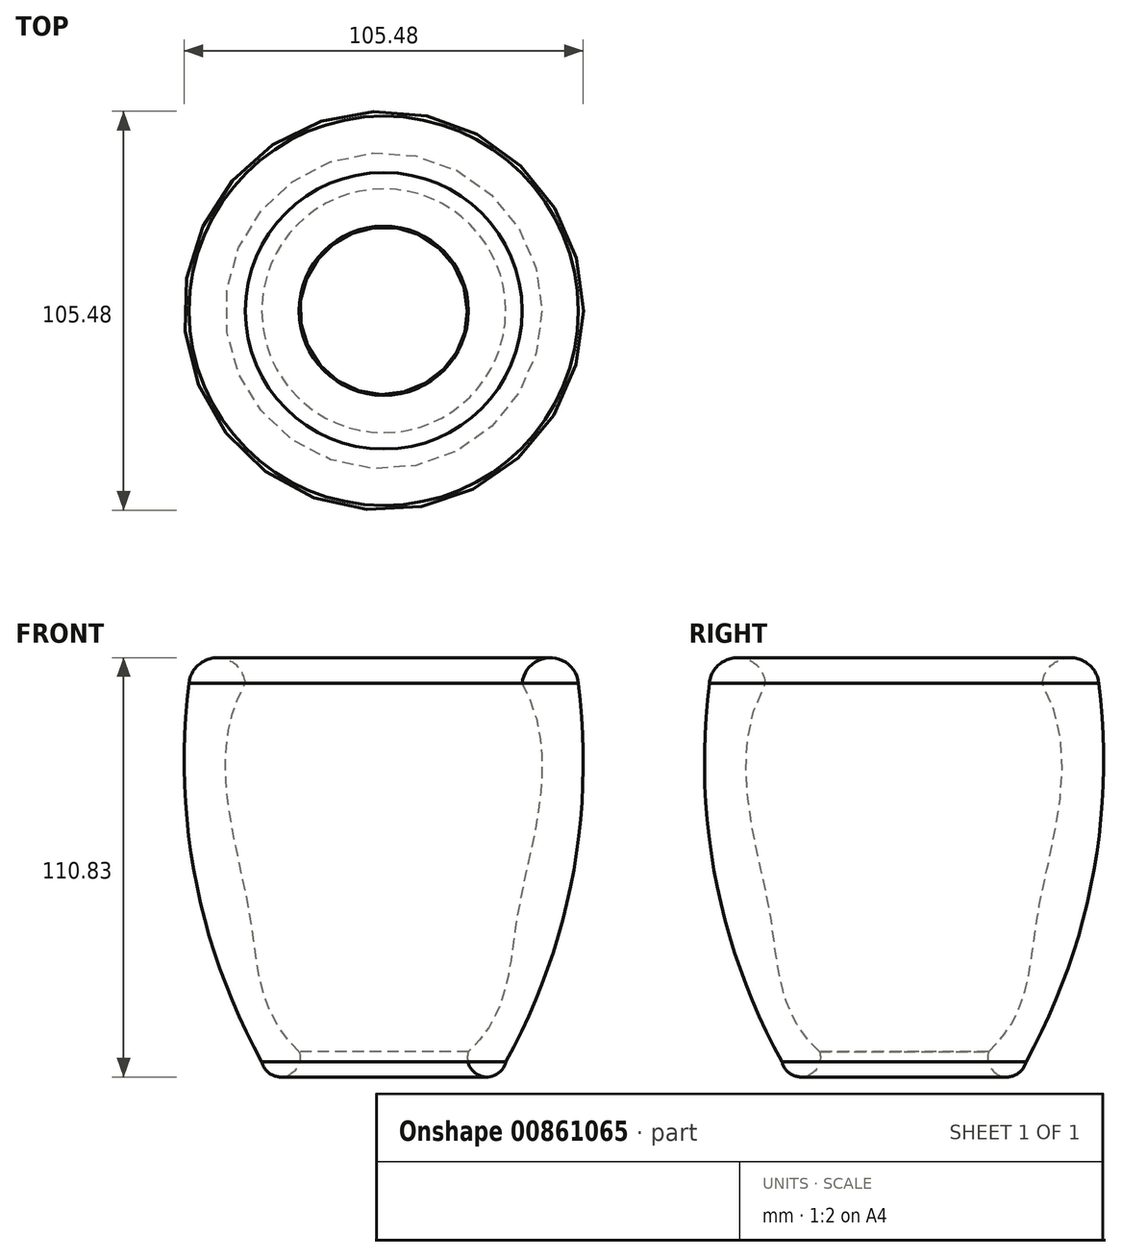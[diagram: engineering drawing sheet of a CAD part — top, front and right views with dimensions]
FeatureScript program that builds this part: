
annotation { "Feature Type Name" : "Feature", "Feature Type Description" : "" }
export const myFeature = defineFeature(function(context is Context, id is Id, definition is map)
    precondition{}
    {
        {
            var Q0;
            Q0=qCreatedBy(makeId("Front.planeOp"),FACE);
            var sketch = newSketch(context, id + "F0", { "sketchPlane" : qUnion([Q0])});
            skArc(sketch, "E0", {"start": v(-36.56, 47.04) * mm, "mid": v(-44, 53.78) * mm, "end": v(-51.46, 47.04) * mm});
            skLineSegment(sketch, "E1", {"start": v(0, 0) * mm, "end": v(0, -38.02) * mm});
            skFitSpline(sketch, "E2", {"points": [v(-36.56, 47.04) * mm, v(-35.55, -12.93) * mm, v(-22.35, -50.4) * mm], "startDerivative": vector(-58.46, -104.82) * mm, "endDerivative": vector(76.84, -72.7) * mm});
            skArc(sketch, "E3", {"start": v(-51.46, 47.04) * mm, "mid": v(-49.8, -4.52) * mm, "end": v(-32.23, -53.03) * mm});
            skArc(sketch, "E4", {"start": v(-32.23, -53.03) * mm, "mid": v(-25.92, -56.88) * mm, "end": v(-22.35, -50.4) * mm});
            skSolve(sketch);
        }
        {
            var Q0;
            Q0 = qSketchRegion(id + "F0", true);
            var Q1;
            Q1=sQuery(id+"F0.wireOp",EDGE,"E1");
            revolve(context, id + "F1", {"surfaceOperationType" : NewSurfaceOperationType.NEW, "entities" : qUnion([Q0]), "axis" : qUnion([Q1]), "revolveType" : RevolveType.FULL});
        }
    });
